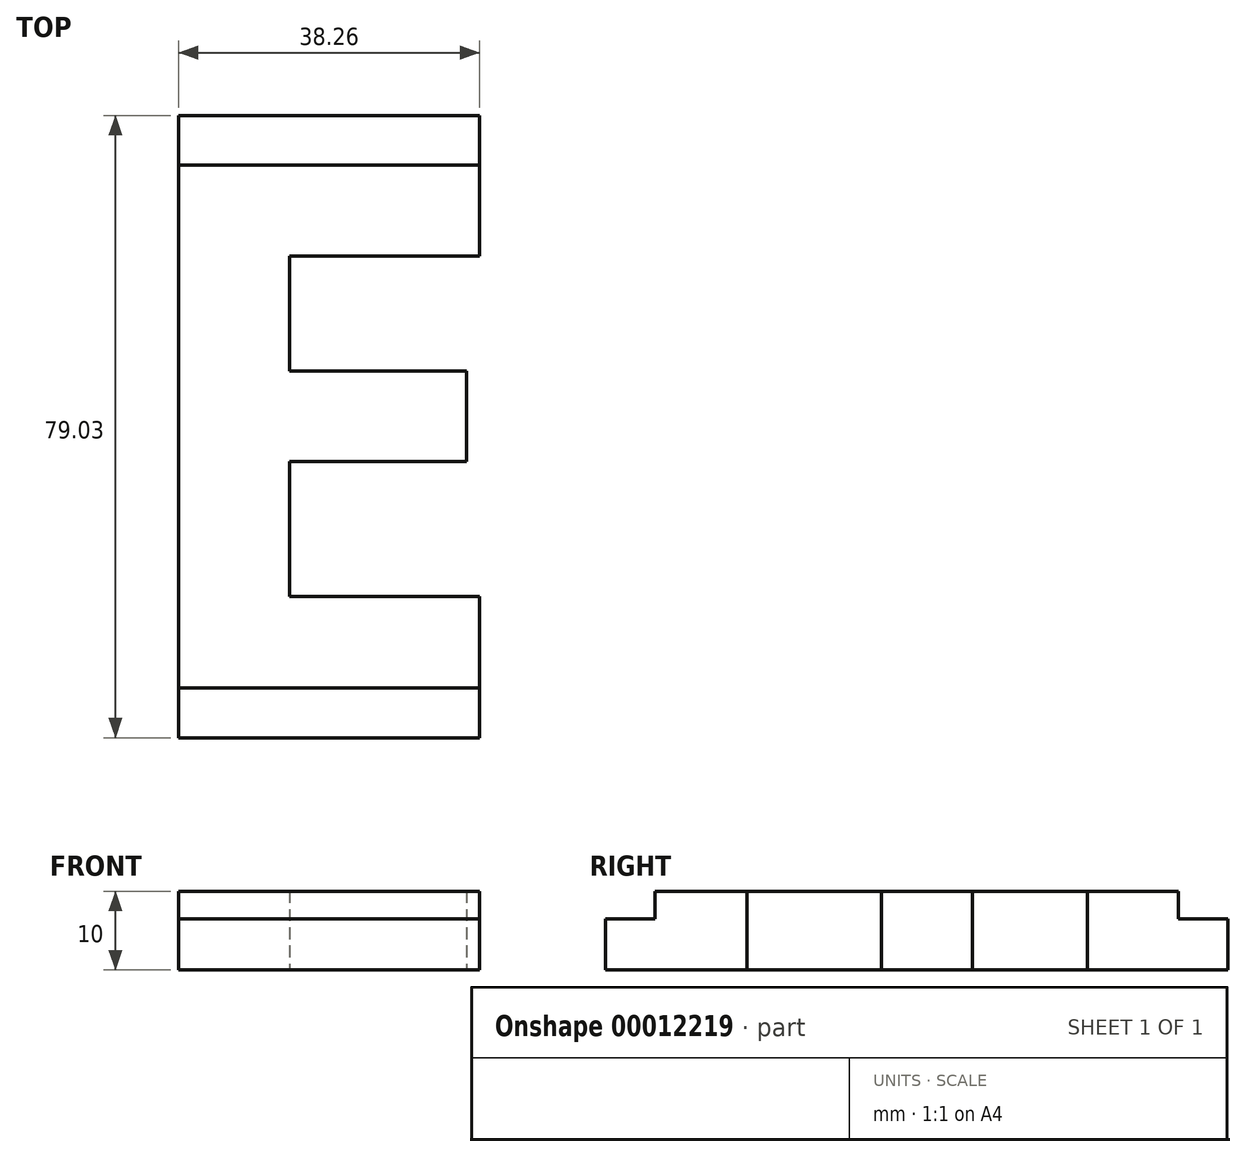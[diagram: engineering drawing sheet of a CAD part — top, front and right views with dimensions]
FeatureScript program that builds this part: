
annotation { "Feature Type Name" : "Feature", "Feature Type Description" : "" }
export const myFeature = defineFeature(function(context is Context, id is Id, definition is map)
    precondition{}
    {
        {
            var Q0;
            Q0=qCreatedBy(makeId("Top.planeOp"),FACE);
            var sketch = newSketch(context, id + "F0", { "sketchPlane" : qUnion([Q0])});
            skText(sketch, "E0", { "text": "E", "fontName": "OpenSans-Bold.ttf"});
            const initialGuessF0  = {"E0": [-0.04662, 0, 1, 0, 0.067]};
            skSetInitialGuess(sketch, initialGuessF0);
            skSolve(sketch);
        }
        {
            var Q0;
            Q0=makeQuery(id+"F0.imprint","IMPRINT",FACE,{"disambiguationData":[TD([[makeQuery(id+"F0.imprint","IMPRINT",EDGE,{"derivedFrom":sQuery(id+"F0.wireOp",EDGE,"E0.sketch_text.stroke-0")}),-1.0]])]});
            extrude(context, id + "F1", {"entities" : qUnion([Q0]), "depth" : 10 * mm});
        }
        {
            var Q0;
            Q0=makeQuery(id+"F1.opExtrude","SWEPT_FACE",FACE,{"disambiguationData":[OSD([sQuery(id+"F0.wireOp",EDGE,"E0.sketch_text.stroke-0")])]});
            var sketch = newSketch(context, id + "F2", { "sketchPlane" : qUnion([Q0])});
            skLineSegment(sketch, "E1.0.0", {"start": v(-38.25, 0) * mm, "end": v(0, 0) * mm});
            skLineSegment(sketch, "E1.0.1", {"start": v(0, 0) * mm, "end": v(0, 10) * mm});
            skLineSegment(sketch, "E1.0.2", {"start": v(0, 10) * mm, "end": v(-38.25, 10) * mm});
            skLineSegment(sketch, "E1.0.3", {"start": v(-38.25, 10) * mm, "end": v(-38.25, 0) * mm});
            skLineSegment(sketch, "E2.top", {"start": v(-38.25, 6.5) * mm, "end": v(0, 6.5) * mm});
            skLineSegment(sketch, "E2.left", {"start": v(-38.25, 0) * mm, "end": v(-38.25, 6.5) * mm});
            skLineSegment(sketch, "E2.right", {"start": v(0, 0) * mm, "end": v(0, 6.5) * mm});
            skSolve(sketch);
        }
        {
            var Q0;
            Q0=makeQuery(id+"F2.imprint","IMPRINT",FACE,{"disambiguationData":[TD([[makeQuery(id+"F2.imprint","IMPRINT",EDGE,{"derivedFrom":sQuery(id+"F2.wireOp",EDGE,"E1.0.0")}),-1.0]])]});
            extrude(context, id + "F3", {"entities" : qUnion([Q0]), "operationType" : NewBodyOperationType.ADD, "depth" : 6.3 * mm});
        }
        {
            var Q0;
            Q0=makeQuery(id+"F1.opExtrude","SWEPT_FACE",FACE,{"disambiguationData":[OSD([sQuery(id+"F0.wireOp",EDGE,"E0.sketch_text.stroke-2")])]});
            var sketch = newSketch(context, id + "F4", { "sketchPlane" : qUnion([Q0])});
            skLineSegment(sketch, "E3.0.0", {"start": v(0, 0) * mm, "end": v(38.25, 0) * mm});
            skLineSegment(sketch, "E3.0.1", {"start": v(38.25, 0) * mm, "end": v(38.25, 10) * mm});
            skLineSegment(sketch, "E3.0.2", {"start": v(38.25, 10) * mm, "end": v(0, 10) * mm});
            skLineSegment(sketch, "E3.0.3", {"start": v(0, 10) * mm, "end": v(0, 0) * mm});
            skLineSegment(sketch, "E4.top", {"start": v(0, 6.5) * mm, "end": v(38.25, 6.5) * mm});
            skLineSegment(sketch, "E4.left", {"start": v(0, 0) * mm, "end": v(0, 6.5) * mm});
            skLineSegment(sketch, "E4.right", {"start": v(38.25, 0) * mm, "end": v(38.25, 6.5) * mm});
            skSolve(sketch);
        }
        {
            var Q0;
            Q0=makeQuery(id+"F4.imprint","IMPRINT",FACE,{"disambiguationData":[TD([[makeQuery(id+"F4.imprint","IMPRINT",EDGE,{"derivedFrom":sQuery(id+"F4.wireOp",EDGE,"E3.0.0")}),-1.0]])]});
            extrude(context, id + "F5", {"entities" : qUnion([Q0]), "operationType" : NewBodyOperationType.ADD, "depth" : 6.3 * mm});
        }
    });
